# Revit family: Distanzbügel_150_FS_FT
name_source: partatom
category: Generic Models
revit_build: Autodesk Revit 2017 (Build: 20160225_1515(x64)
units: mm (PartAtom-declared; Revit-internal decimal feet)

## family parameters
Always vertical = Yes
Can host rebar = No
Cut with Voids When Loaded = No
Part Type = Normal
Room Calculation Point = No
Round Connector Dimension = Use Diameter
Shared = No
Work Plane-Based = No

## types (2) — shared parameters
Cut's number = 2
Cut's space = 100 mm  [stored 0.328084 ft]
Length = 30 mm  [stored 0.0984252 ft]
Manufacturer = OBO BETTERMANN
URL = http://www.obo-bettermann.com
Width = 150 mm
Width 1 = 75 mm

## per-type parameters (varying)
| type | GTIN | Manufacturer Art.No. | Material |
| DBLG 20 150 FS | 4012196279371 | 6015658 | Strip-galvanised |
| DBLG 20 150 FT | 4012196043088 | 6015660 | Hot-dip galvanised |

note: column(s) folded — value = type name in every type: Article Type

note: [stored X ft] marks values corroborated as IEEE doubles in the binary element streams (Revit-internal decimal feet)

## geometry (parser evidence)
native form markers: Sweep x2
no freeform markers — native parametric forms only
